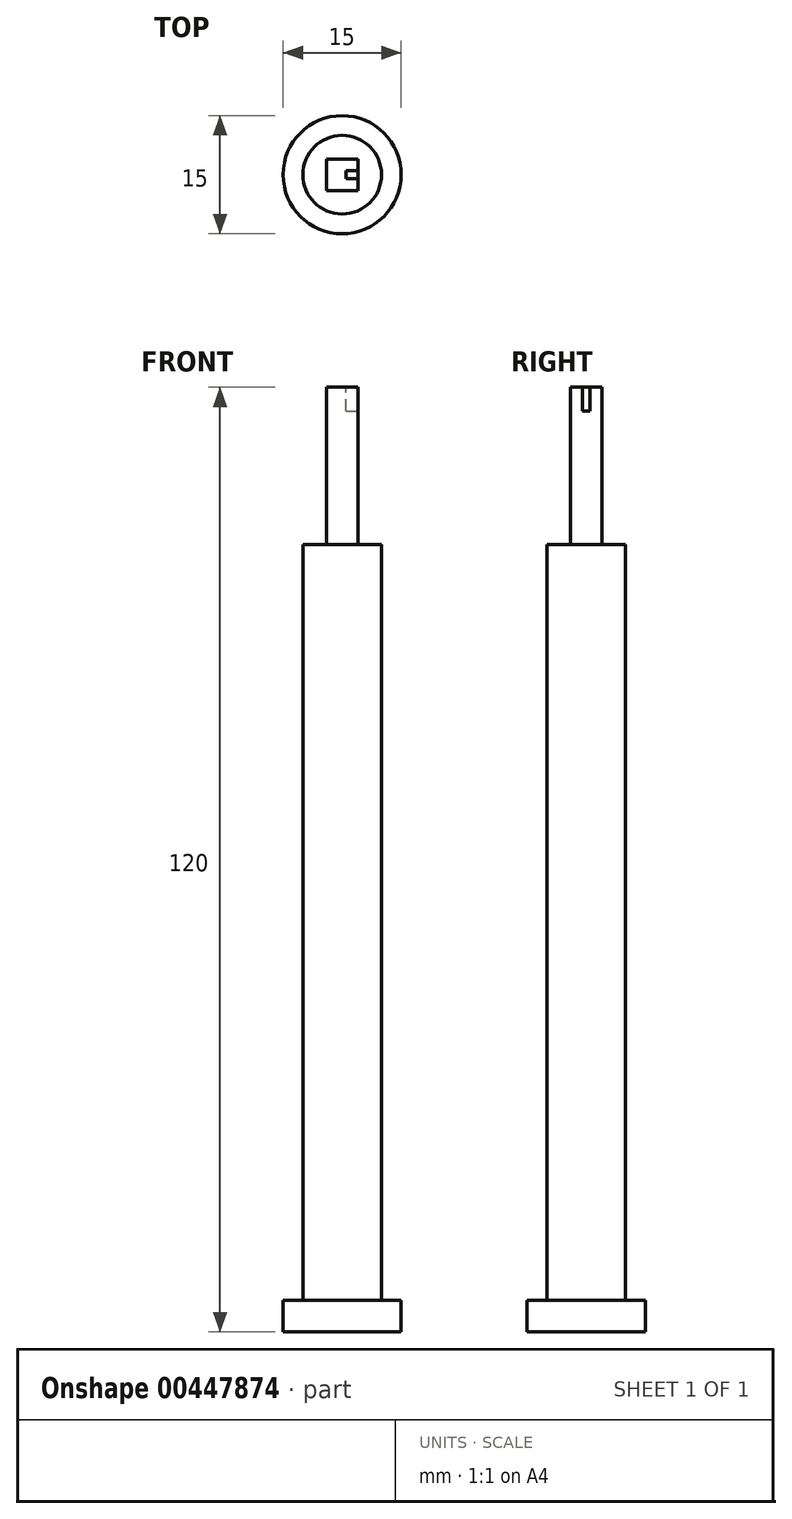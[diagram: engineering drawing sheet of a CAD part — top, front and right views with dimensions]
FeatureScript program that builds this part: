
annotation { "Feature Type Name" : "Feature", "Feature Type Description" : "" }
export const myFeature = defineFeature(function(context is Context, id is Id, definition is map)
    precondition{}
    {
        {
            var Q0;
            Q0=qCreatedBy(makeId("Top.planeOp"),FACE);
            var sketch = newSketch(context, id + "F0", { "sketchPlane" : qUnion([Q0])});
            skCircle(sketch, "E0", {"center": v(0, 0) * mm, "radius": 7.5 * mm});
            skSolve(sketch);
        }
        {
            var Q0;
            Q0=qSketchRegion(id+"F0",true);
            extrude(context, id + "F1", {"entities" : qUnion([Q0]), "depth" : 4 * mm});
        }
        {
            var Q0;
            Q0=qCreatedBy(makeId("Top.planeOp"),FACE);
            var sketch = newSketch(context, id + "F2", { "sketchPlane" : qUnion([Q0])});
            skCircle(sketch, "E1", {"center": v(0, 0) * mm, "radius": 5 * mm});
            skSolve(sketch);
        }
        {
            var Q0;
            Q0=qSketchRegion(id+"F2",true);
            extrude(context, id + "F3", {"entities" : qUnion([Q0]), "operationType" : NewBodyOperationType.ADD, "depth" : 100 * mm});
        }
        {
            var Q0;
            Q0=makeQuery(id+"F3.opExtrude","CAP_FACE",FACE,{"disambiguationData":[OSD([sQuery(id+"F2.wireOp",EDGE,"E1")])],"isStart":false});
            var sketch = newSketch(context, id + "F4", { "sketchPlane" : qUnion([Q0])});
            skLineSegment(sketch, "E2.bottom", {"start": v(-2, 2) * mm, "end": v(2, 2) * mm});
            skLineSegment(sketch, "E2.top", {"start": v(-2, -2) * mm, "end": v(2, -2) * mm});
            skLineSegment(sketch, "E2.left", {"start": v(-2, 2) * mm, "end": v(-2, -2) * mm});
            skLineSegment(sketch, "E2.right", {"start": v(2, 2) * mm, "end": v(2, -2) * mm});
            skSolve(sketch);
        }
        {
            var Q0;
            Q0=makeQuery(id+"F4.imprint","IMPRINT",FACE,{"disambiguationData":[TD([[makeQuery(id+"F4.imprint","IMPRINT",EDGE,{"derivedFrom":sQuery(id+"F4.wireOp",EDGE,"E2.bottom")}),-1.0]])]});
            extrude(context, id + "F5", {"entities" : qUnion([Q0]), "operationType" : NewBodyOperationType.ADD, "depth" : 20 * mm});
        }
        {
            var Q0;
            Q0=makeQuery(id+"F5.opExtrude","CAP_FACE",FACE,{"disambiguationData":[OSD([sQuery(id+"F4.wireOp",EDGE,"E2.bottom"),sQuery(id+"F4.wireOp",EDGE,"E2.top"),sQuery(id+"F4.wireOp",EDGE,"E2.left"),sQuery(id+"F4.wireOp",EDGE,"E2.right")])],"isStart":false});
            var sketch = newSketch(context, id + "F6", { "sketchPlane" : qUnion([Q0])});
            skLineSegment(sketch, "E3.bottom", {"start": v(0.5, 0.5) * mm, "end": v(2.76, 0.5) * mm});
            skLineSegment(sketch, "E3.top", {"start": v(0.5, -0.5) * mm, "end": v(2.76, -0.5) * mm});
            skLineSegment(sketch, "E3.left", {"start": v(0.5, 0.5) * mm, "end": v(0.5, -0.5) * mm});
            skLineSegment(sketch, "E3.right", {"start": v(2.76, 0.5) * mm, "end": v(2.76, -0.5) * mm});
            skSolve(sketch);
        }
        {
            var Q0;
            Q0 = qSketchRegion(id + "F6", true);
            extrude(context, id + "F7", {"entities" : qUnion([Q0]), "operationType" : NewBodyOperationType.REMOVE, "oppositeDirection" : true, "depth" : 3 * mm});
        }
    });
